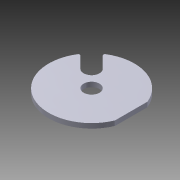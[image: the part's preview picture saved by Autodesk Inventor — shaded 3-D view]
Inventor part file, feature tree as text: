
AUTODESK INVENTOR PART (.ipt)
format: ipt  version: 2013 (Build 170138000, 138)  size: 99,840 bytes
history: native  units: mm
features: extrude x1, sketch x1
ambient origin geometry x8: Origin, YZ Plane, XZ Plane, XY Plane, X Axis, Y Axis, Z Axis, Center Point
feature tree (2):
  extrude  "Extrusion3"  Depth=20.0mm
  sketch  "Sketch1"  dims[d0=108.0mm d1=20.0mm d4=20.0mm d12=50.0mm d13=2.0mm d14=54.0mm d15=54.0mm d16=20.0mm d17=6.0mm d18=0.0mm d19=45.0deg d21=10.0mm d22=30.0mm]
